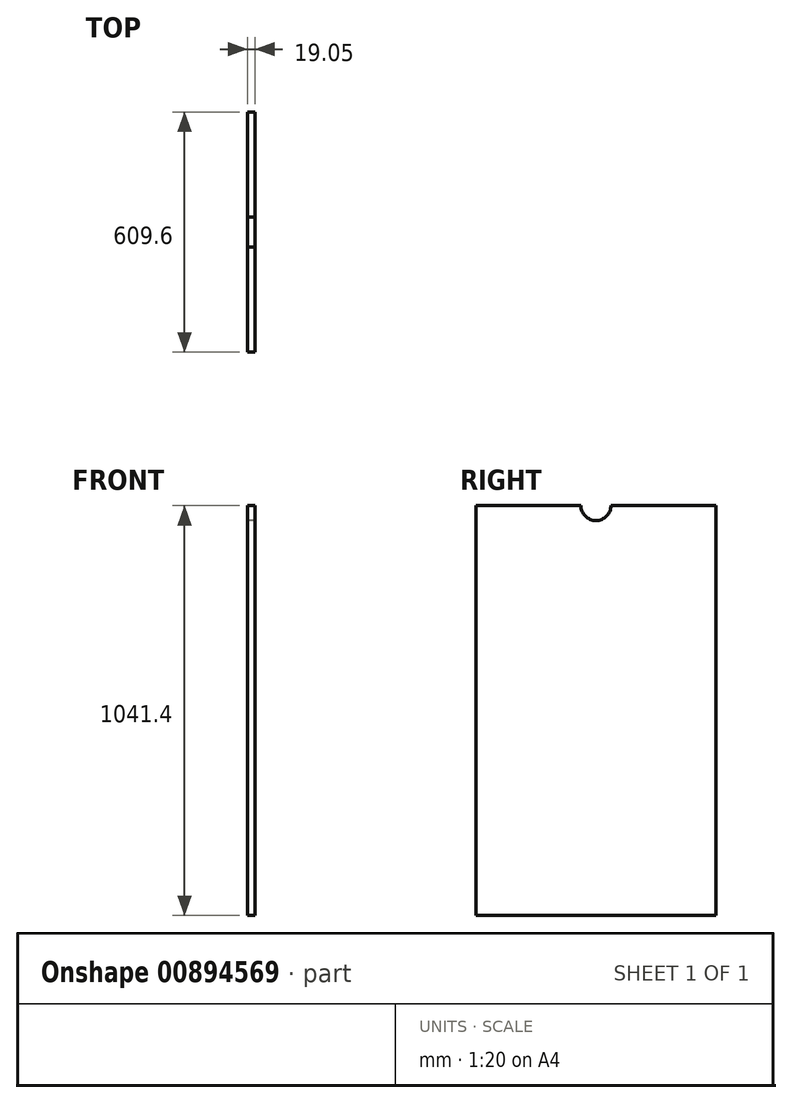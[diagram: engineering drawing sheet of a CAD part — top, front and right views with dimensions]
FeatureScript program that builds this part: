
annotation { "Feature Type Name" : "Feature", "Feature Type Description" : "" }
export const myFeature = defineFeature(function(context is Context, id is Id, definition is map)
    precondition{}
    {
        {
            var Q0;
            Q0=qCreatedBy(makeId("Right.planeOp"),FACE);
            var sketch = newSketch(context, id + "F0", { "sketchPlane" : qUnion([Q0])});
            skLineSegment(sketch, "E0.bottom", {"start": v(304.8, 520.7) * mm, "end": v(-304.8, 520.7) * mm});
            skLineSegment(sketch, "E0.top", {"start": v(304.8, -520.7) * mm, "end": v(-304.8, -520.7) * mm});
            skLineSegment(sketch, "E0.left", {"start": v(304.8, 520.7) * mm, "end": v(304.8, -520.7) * mm});
            skLineSegment(sketch, "E0.right", {"start": v(-304.8, 520.7) * mm, "end": v(-304.8, -520.7) * mm});
            skPoint(sketch, "E0.middle", {"position": v(0, 0) * mm});
            skCircle(sketch, "E1", {"center": v(0, 520.7) * mm, "radius": 38.1 * mm});
            skSolve(sketch);
        }
        {
            var Q0;
            Q0=makeQuery(id+"F0.imprint","IMPRINT",FACE,{"disambiguationData":[TD([[makeQuery(id+"F0.imprint","IMPRINT",EDGE,{"derivedFrom":sQuery(id+"F0.wireOp",EDGE,"E0.top")}),-1.0]])]});
            extrude(context, id + "F1", {"entities" : qUnion([Q0]), "depth" : 19.05 * mm, "offsetDistance" : 25.4 * mm});
        }
    });
